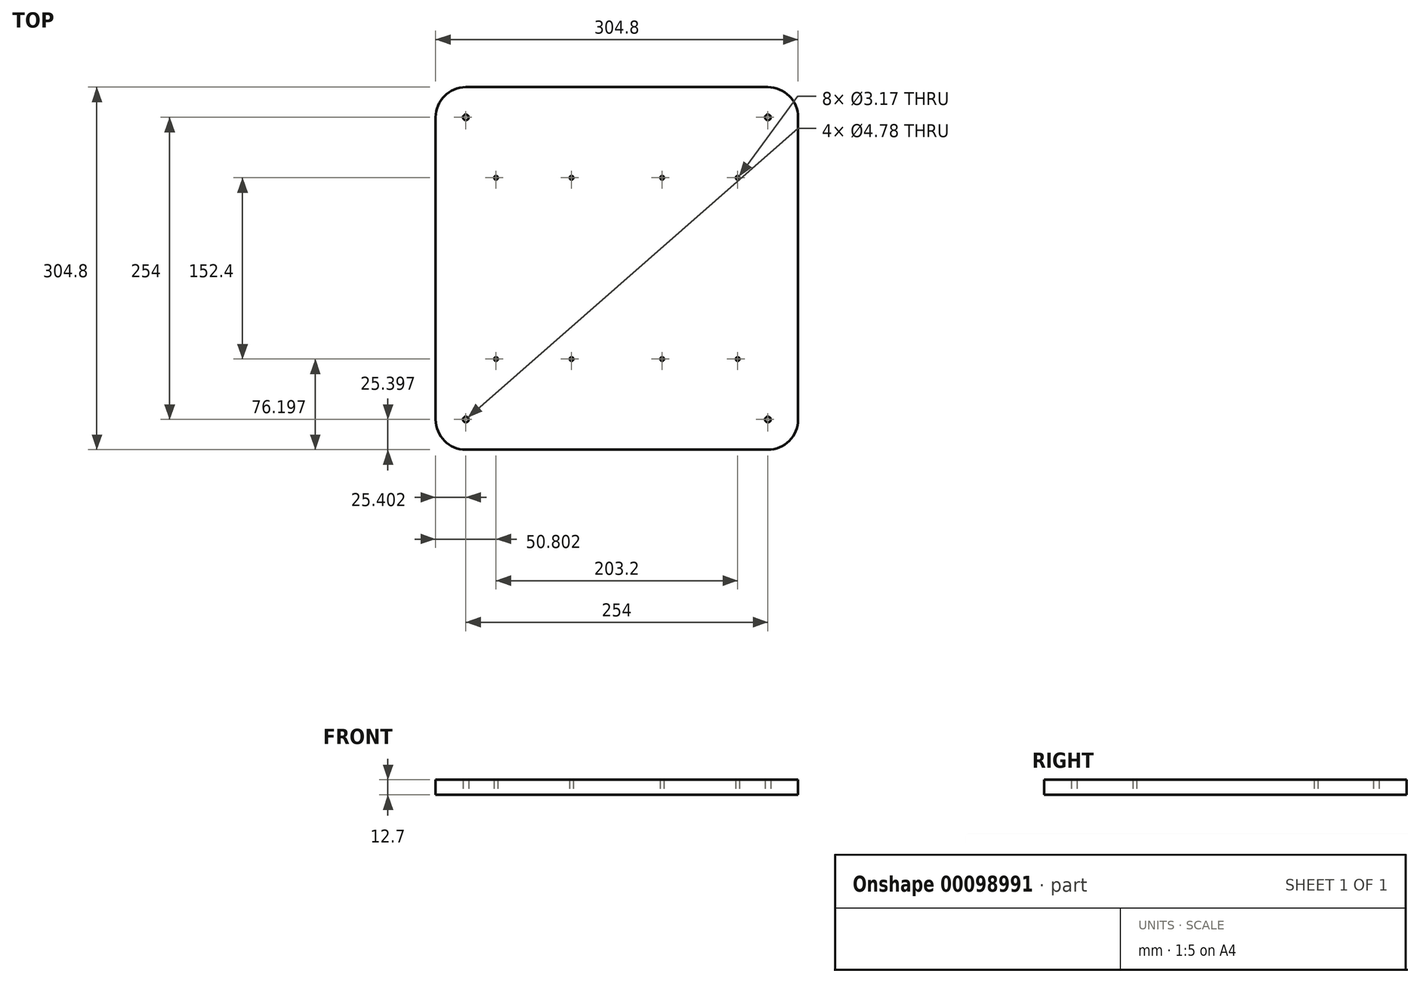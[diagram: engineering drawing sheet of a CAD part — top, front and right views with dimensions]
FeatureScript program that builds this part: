
annotation { "Feature Type Name" : "Feature", "Feature Type Description" : "" }
export const myFeature = defineFeature(function(context is Context, id is Id, definition is map)
    precondition{}
    {
        {
            var Q0;
            Q0=qCreatedBy(makeId("Top.planeOp"),FACE);
            var sketch = newSketch(context, id + "F0", { "sketchPlane" : qUnion([Q0])});
            skLineSegment(sketch, "E0.bottom", {"start": v(-191.92, 145.1) * mm, "end": v(62.08, 145.1) * mm});
            skLineSegment(sketch, "E0.top", {"start": v(-191.92, -159.7) * mm, "end": v(62.08, -159.7) * mm});
            skLineSegment(sketch, "E0.left", {"start": v(-217.32, 119.7) * mm, "end": v(-217.32, -134.3) * mm});
            skLineSegment(sketch, "E0.right", {"start": v(87.48, 119.7) * mm, "end": v(87.48, -134.3) * mm});
            skPoint(sketch, "E1.visualSharp", {"position": v(-217.32, 145.1) * mm});
            skArc(sketch, "E1.filletArc", {"start": v(-191.92, 145.1) * mm, "mid": v(-209.88, 137.67) * mm, "end": v(-217.32, 119.7) * mm});
            skPoint(sketch, "E2.visualSharp", {"position": v(87.48, 145.1) * mm});
            skArc(sketch, "E2.filletArc", {"start": v(87.48, 119.7) * mm, "mid": v(80.04, 137.67) * mm, "end": v(62.08, 145.1) * mm});
            skPoint(sketch, "E3.visualSharp", {"position": v(87.48, -159.7) * mm});
            skArc(sketch, "E3.filletArc", {"start": v(62.08, -159.7) * mm, "mid": v(80.04, -152.25) * mm, "end": v(87.48, -134.3) * mm});
            skPoint(sketch, "E4.visualSharp", {"position": v(-217.32, -159.7) * mm});
            skArc(sketch, "E4.filletArc", {"start": v(-217.32, -134.3) * mm, "mid": v(-209.88, -152.25) * mm, "end": v(-191.92, -159.7) * mm});
            skPoint(sketch, "E5", {"position": v(-166.52, -83.5) * mm});
            skPoint(sketch, "E6", {"position": v(-103.02, -83.5) * mm});
            skPoint(sketch, "E7", {"position": v(-26.82, -83.5) * mm});
            skPoint(sketch, "E8", {"position": v(36.68, -83.5) * mm});
            skPoint(sketch, "E9", {"position": v(-166.52, 68.9) * mm});
            skPoint(sketch, "E10", {"position": v(-103.02, 68.9) * mm});
            skPoint(sketch, "E11", {"position": v(-26.82, 68.9) * mm});
            skPoint(sketch, "E12", {"position": v(36.68, 68.9) * mm});
            skSolve(sketch);
        }
        {
            var Q0;
            Q0=makeQuery(id+"F0.imprint","IMPRINT",FACE,{"disambiguationData":[TD([[makeQuery(id+"F0.imprint","IMPRINT",EDGE,{"derivedFrom":sQuery(id+"F0.wireOp",EDGE,"E0.bottom")}),-1.0]])]});
            extrude(context, id + "F1", {"entities" : qUnion([Q0]), "depth" : 12.7 * mm});
        }
        {
            var Q0;
            Q0=sQuery(id+"F0.wireOp",VERTEX,"E1.filletArc.center");
            var Q1;
            Q1=sQuery(id+"F0.wireOp",VERTEX,"E3.filletArc.center");
            var Q2;
            Q2=sQuery(id+"F0.wireOp",VERTEX,"E2.filletArc.center");
            var Q3;
            Q3=sQuery(id+"F0.wireOp",VERTEX,"E4.filletArc.center");
            var Q4;
            Q4=makeQuery(id+"F1.opExtrude","SWEPT_BODY",BODY,{"disambiguationData":[OSD([sQuery(id+"F0.wireOp",EDGE,"E0.bottom"),sQuery(id+"F0.wireOp",EDGE,"E0.top"),sQuery(id+"F0.wireOp",EDGE,"E0.left"),sQuery(id+"F0.wireOp",EDGE,"E0.right"),sQuery(id+"F0.wireOp",EDGE,"E1.filletArc"),sQuery(id+"F0.wireOp",EDGE,"E2.filletArc"),sQuery(id+"F0.wireOp",EDGE,"E3.filletArc"),sQuery(id+"F0.wireOp",EDGE,"E4.filletArc")])]});
            hole(context, id + "F2", {"style" : HoleStyle.SIMPLE, "endStyle" : HoleEndStyle.THROUGH, "oppositeDirection" : true, "holeDiameter" : 4.78 * mm, "locations" : qUnion([Q0, Q1, Q2, Q3]), "scope" : qUnion([Q4]), "isTappedThrough" : true});
        }
        {
            var Q0;
            Q0=sQuery(id+"F0.wireOp",VERTEX,"E11");
            var Q1;
            Q1=sQuery(id+"F0.wireOp",VERTEX,"E10");
            var Q2;
            Q2=sQuery(id+"F0.wireOp",VERTEX,"E9");
            var Q3;
            Q3=sQuery(id+"F0.wireOp",VERTEX,"E5");
            var Q4;
            Q4=sQuery(id+"F0.wireOp",VERTEX,"E6");
            var Q5;
            Q5=sQuery(id+"F0.wireOp",VERTEX,"E7");
            var Q6;
            Q6=sQuery(id+"F0.wireOp",VERTEX,"E8");
            var Q7;
            Q7=sQuery(id+"F0.wireOp",VERTEX,"E12");
            var Q8;
            Q8=makeQuery(id+"F1.opExtrude","SWEPT_BODY",BODY,{"disambiguationData":[OSD([sQuery(id+"F0.wireOp",EDGE,"E0.bottom"),sQuery(id+"F0.wireOp",EDGE,"E0.top"),sQuery(id+"F0.wireOp",EDGE,"E0.left"),sQuery(id+"F0.wireOp",EDGE,"E0.right"),sQuery(id+"F0.wireOp",EDGE,"E1.filletArc"),sQuery(id+"F0.wireOp",EDGE,"E2.filletArc"),sQuery(id+"F0.wireOp",EDGE,"E3.filletArc"),sQuery(id+"F0.wireOp",EDGE,"E4.filletArc")])]});
            hole(context, id + "F3", {"style" : HoleStyle.SIMPLE, "endStyle" : HoleEndStyle.THROUGH, "oppositeDirection" : true, "holeDiameter" : 3.17 * mm, "locations" : qUnion([Q0, Q1, Q2, Q3, Q4, Q5, Q6, Q7]), "scope" : qUnion([Q8]), "isTappedThrough" : true});
        }
    });
